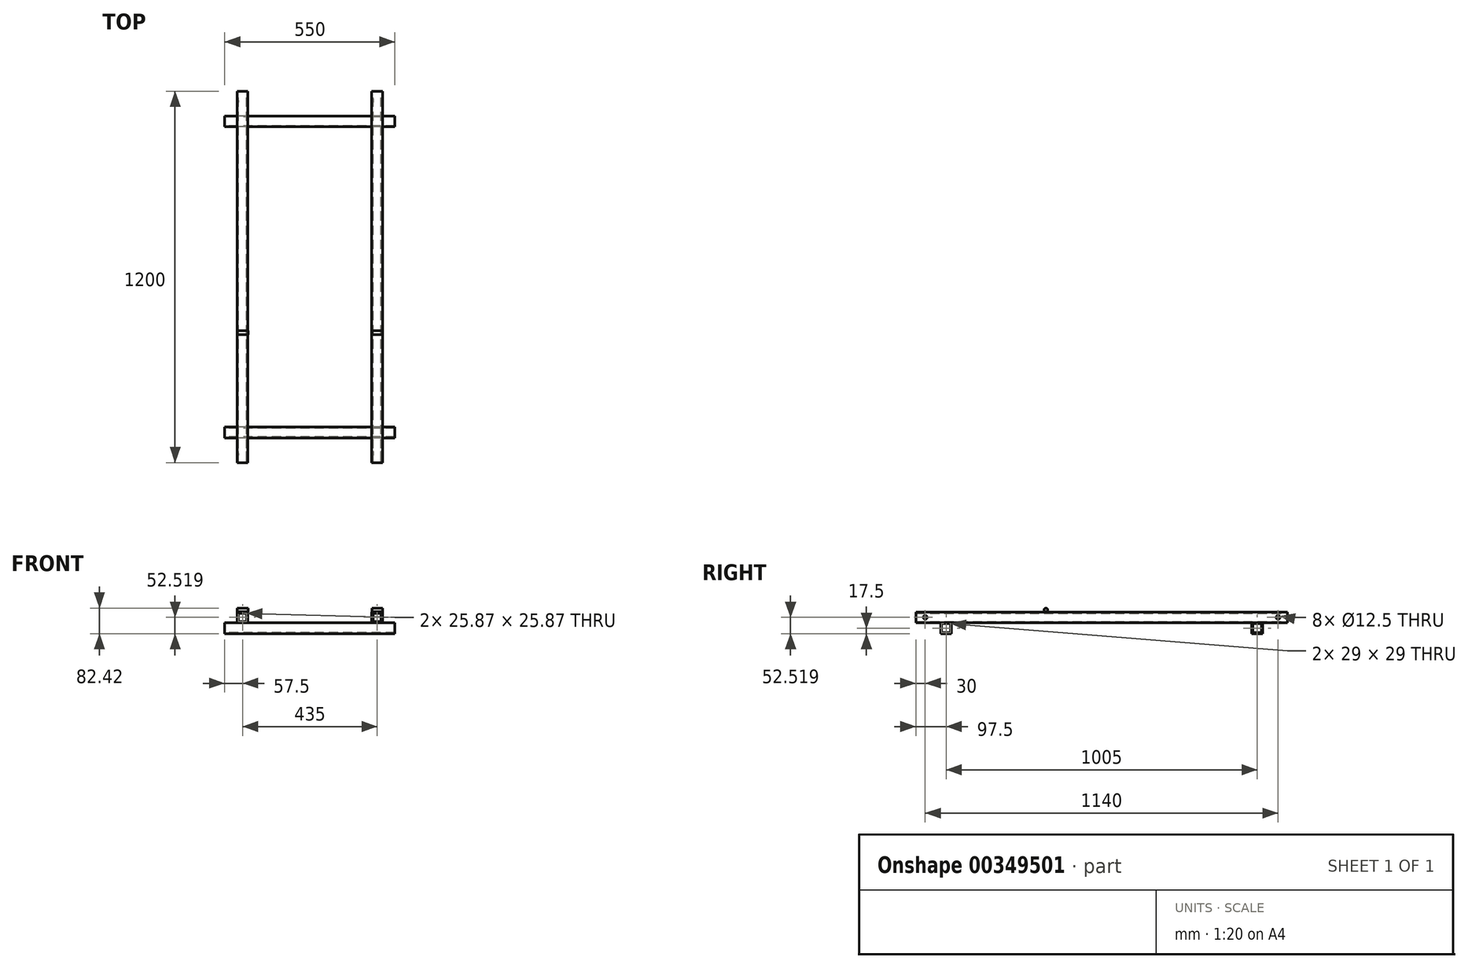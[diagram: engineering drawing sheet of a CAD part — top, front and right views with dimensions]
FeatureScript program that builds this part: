
annotation { "Feature Type Name" : "Feature", "Feature Type Description" : "" }
export const myFeature = defineFeature(function(context is Context, id is Id, definition is map)
    precondition{}
    {
        {
            var Q0;
            Q0=qCreatedBy(makeId("Front.planeOp"),FACE);
            var sketch = newSketch(context, id + "F0", { "sketchPlane" : qUnion([Q0])});
            skLineSegment(sketch, "E0.bottom", {"start": v(-235, -15.2) * mm, "end": v(-200, -15.2) * mm});
            skLineSegment(sketch, "E0.top", {"start": v(-235, -50.2) * mm, "end": v(-200, -50.2) * mm});
            skLineSegment(sketch, "E0.left", {"start": v(-235, -15.2) * mm, "end": v(-235, -50.2) * mm});
            skLineSegment(sketch, "E0.right", {"start": v(-200, -15.2) * mm, "end": v(-200, -50.2) * mm});
            skLineSegment(sketch, "E1.0", {"start": v(-230.44, -45.64) * mm, "end": v(-204.56, -45.64) * mm});
            skLineSegment(sketch, "E1.1", {"start": v(-230.44, -19.76) * mm, "end": v(-230.44, -45.64) * mm});
            skLineSegment(sketch, "E1.2", {"start": v(-230.44, -19.76) * mm, "end": v(-204.56, -19.76) * mm});
            skLineSegment(sketch, "E1.3", {"start": v(-204.56, -19.76) * mm, "end": v(-204.56, -45.64) * mm});
            skLineSegment(sketch, "E2.MirrorCS", {"start": v(235, -50.2) * mm, "end": v(200, -50.2) * mm});
            skLineSegment(sketch, "E3.MirrorCS", {"start": v(230.44, -45.64) * mm, "end": v(204.56, -45.64) * mm});
            skLineSegment(sketch, "E4.MirrorCS", {"start": v(235, -15.2) * mm, "end": v(200, -15.2) * mm});
            skLineSegment(sketch, "E5.MirrorCS", {"start": v(204.56, -19.76) * mm, "end": v(204.56, -45.64) * mm});
            skLineSegment(sketch, "E6.MirrorCS", {"start": v(230.44, -19.76) * mm, "end": v(204.56, -19.76) * mm});
            skLineSegment(sketch, "E7.MirrorCS", {"start": v(235, -15.2) * mm, "end": v(235, -50.2) * mm});
            skLineSegment(sketch, "E8.MirrorCS", {"start": v(200, -15.2) * mm, "end": v(200, -50.2) * mm});
            skLineSegment(sketch, "E9.MirrorCS", {"start": v(230.44, -19.76) * mm, "end": v(230.44, -45.64) * mm});
            skSolve(sketch);
        }
        {
            var Q0;
            Q0=qCreatedBy(makeId("Right.planeOp"),FACE);
            var sketch = newSketch(context, id + "F1", { "sketchPlane" : qUnion([Q0])});
            skLineSegment(sketch, "E10.bottom", {"start": v(520, -50.22) * mm, "end": v(485, -50.22) * mm});
            skLineSegment(sketch, "E10.top", {"start": v(520, -85.22) * mm, "end": v(485, -85.22) * mm});
            skLineSegment(sketch, "E10.left", {"start": v(520, -50.22) * mm, "end": v(520, -85.22) * mm});
            skLineSegment(sketch, "E10.right", {"start": v(485, -50.22) * mm, "end": v(485, -85.22) * mm});
            skLineSegment(sketch, "E11.0", {"start": v(517, -82.22) * mm, "end": v(488, -82.22) * mm});
            skLineSegment(sketch, "E11.1", {"start": v(517, -53.22) * mm, "end": v(517, -82.22) * mm});
            skLineSegment(sketch, "E11.2", {"start": v(517, -53.22) * mm, "end": v(488, -53.22) * mm});
            skLineSegment(sketch, "E11.3", {"start": v(488, -53.22) * mm, "end": v(488, -82.22) * mm});
            skLineSegment(sketch, "E12.MirrorCS", {"start": v(-520, -85.22) * mm, "end": v(-485, -85.22) * mm});
            skLineSegment(sketch, "E13.MirrorCS", {"start": v(-517, -82.22) * mm, "end": v(-488, -82.22) * mm});
            skLineSegment(sketch, "E14.MirrorCS", {"start": v(-520, -50.22) * mm, "end": v(-485, -50.22) * mm});
            skLineSegment(sketch, "E15.MirrorCS", {"start": v(-520, -50.22) * mm, "end": v(-520, -85.22) * mm});
            skLineSegment(sketch, "E16.MirrorCS", {"start": v(-485, -50.22) * mm, "end": v(-485, -85.22) * mm});
            skLineSegment(sketch, "E17.MirrorCS", {"start": v(-488, -53.22) * mm, "end": v(-488, -82.22) * mm});
            skLineSegment(sketch, "E18.MirrorCS", {"start": v(-517, -53.22) * mm, "end": v(-517, -82.22) * mm});
            skLineSegment(sketch, "E19.MirrorCS", {"start": v(-517, -53.22) * mm, "end": v(-488, -53.22) * mm});
            skSolve(sketch);
        }
        {
            var Q0;
            Q0=makeQuery(id+"F0.imprint","IMPRINT",FACE,{"disambiguationData":[TD([[makeQuery(id+"F0.imprint","IMPRINT",EDGE,{"derivedFrom":sQuery(id+"F0.wireOp",EDGE,"E0.bottom")}),-1.0]])]});
            var Q1;
            Q1=makeQuery(id+"F0.imprint","IMPRINT",FACE,{"disambiguationData":[TD([[makeQuery(id+"F0.imprint","IMPRINT",EDGE,{"derivedFrom":sQuery(id+"F0.wireOp",EDGE,"E2.MirrorCS")}),-1.0]])]});
            extrude(context, id + "F2", {"entities" : qUnion([Q0, Q1]), "depth" : 1200 * mm, "symmetric" : true});
        }
        {
            var Q0;
            Q0 = qSketchRegion(id + "F1", true);
            extrude(context, id + "F3", {"entities" : qUnion([Q0]), "depth" : 550 * mm, "symmetric" : true});
        }
        {
            var Q0;
            Q0=makeQuery(id+"F2.opExtrude","SWEPT_FACE",FACE,{"disambiguationData":[OSD([sQuery(id+"F0.wireOp",EDGE,"E0.left")])]});
            var sketch = newSketch(context, id + "F4", { "sketchPlane" : qUnion([Q0])});
            skCircle(sketch, "E20", {"center": v(-570, -32.7) * mm, "radius": 6.25 * mm});
            skCircle(sketch, "E21.MirrorC", {"center": v(570, -32.7) * mm, "radius": 6.25 * mm});
            skSolve(sketch);
        }
        {
            var Q0;
            Q0 = qSketchRegion(id + "F4", true);
            extrude(context, id + "F5", {"entities" : qUnion([Q0]), "operationType" : NewBodyOperationType.REMOVE, "oppositeDirection" : true, "depth" : 501.65 * mm});
        }
        {
            var Q0;
            Q0=makeQuery(id+"F2.opExtrude","SWEPT_FACE",FACE,{"disambiguationData":[OSD([sQuery(id+"F0.wireOp",EDGE,"E7.MirrorCS")])]});
            var sketch = newSketch(context, id + "F6", { "sketchPlane" : qUnion([Q0])});
            skCircle(sketch, "E22", {"center": v(-570, -32.7) * mm, "radius": 6.25 * mm});
            skCircle(sketch, "E23.MirrorC", {"center": v(570, -32.7) * mm, "radius": 6.25 * mm});
            skSolve(sketch);
        }
        {
            var Q0;
            Q0 = qSketchRegion(id + "F6", true);
            extrude(context, id + "F7", {"entities" : qUnion([Q0]), "operationType" : NewBodyOperationType.REMOVE, "oppositeDirection" : true, "depth" : 39.37 * mm});
        }
        {
            var Q0;
            Q0=makeQuery(id+"F2.opExtrude","SWEPT_FACE",FACE,{"disambiguationData":[OSD([sQuery(id+"F0.wireOp",EDGE,"E7.MirrorCS")])]});
            var sketch = newSketch(context, id + "F8", { "sketchPlane" : qUnion([Q0])});
            skCircle(sketch, "E24", {"center": v(-180, -8.8) * mm, "radius": 6 * mm});
            skSolve(sketch);
        }
        {
            var Q0;
            Q0 = qSketchRegion(id + "F8", true);
            extrude(context, id + "F9", {"entities" : qUnion([Q0]), "oppositeDirection" : true, "depth" : 34.8 * mm});
        }
        {
            var Q0;
            Q0=makeQuery(id+"F2.opExtrude","SWEPT_FACE",FACE,{"disambiguationData":[OSD([sQuery(id+"F0.wireOp",EDGE,"E0.left")])]});
            var sketch = newSketch(context, id + "F10", { "sketchPlane" : qUnion([Q0])});
            skCircle(sketch, "E25", {"center": v(179.94, -8.86) * mm, "radius": 6 * mm});
            skSolve(sketch);
        }
        {
            var Q0;
            Q0 = qSketchRegion(id + "F10", true);
            extrude(context, id + "F11", {"entities" : qUnion([Q0]), "oppositeDirection" : true, "depth" : 35.56 * mm});
        }
    });
